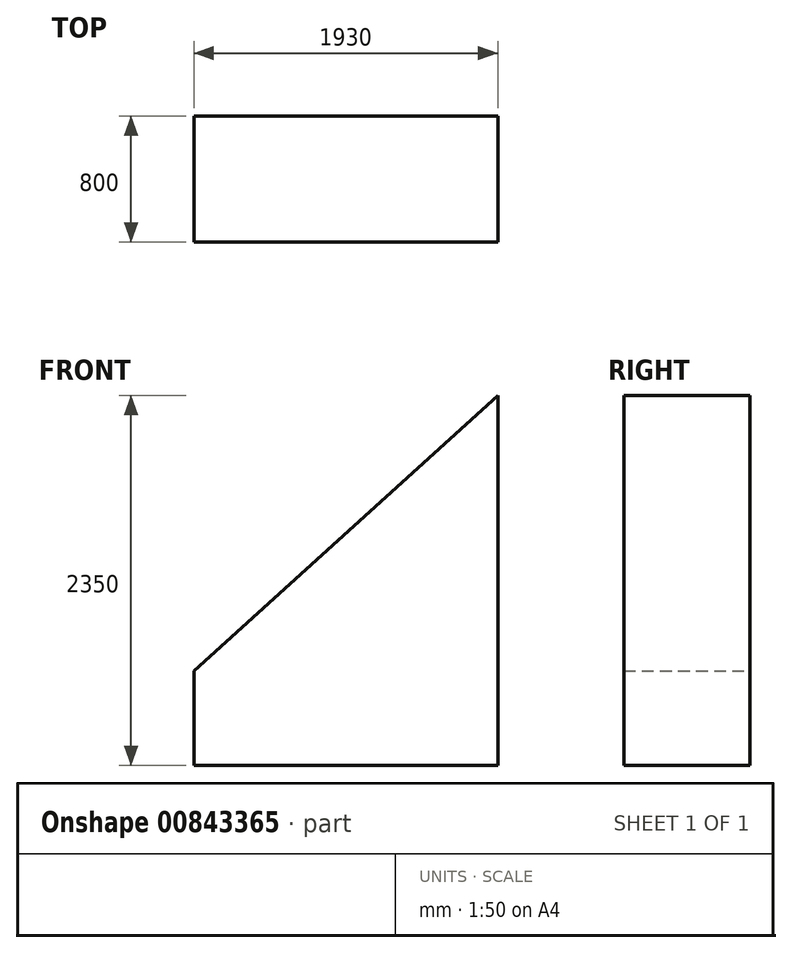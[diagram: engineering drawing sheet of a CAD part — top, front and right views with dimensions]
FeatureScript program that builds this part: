
annotation { "Feature Type Name" : "Feature", "Feature Type Description" : "" }
export const myFeature = defineFeature(function(context is Context, id is Id, definition is map)
    precondition{}
    {
        {
            var Q0;
            Q0=qCreatedBy(makeId("Front.planeOp"),FACE);
            var sketch = newSketch(context, id + "F0", { "sketchPlane" : qUnion([Q0])});
            skLineSegment(sketch, "E0", {"start": v(0, 600) * mm, "end": v(0, 0) * mm});
            skLineSegment(sketch, "E1", {"start": v(0, 0) * mm, "end": v(1930, 0) * mm});
            skLineSegment(sketch, "E2", {"start": v(1930, 2350) * mm, "end": v(0, 600) * mm});
            skLineSegment(sketch, "E3", {"start": v(1930, 2350) * mm, "end": v(1930, 0) * mm});
            skSolve(sketch);
        }
        {
            var Q0;
            Q0=makeQuery(id+"F0.imprint","IMPRINT",FACE,{"disambiguationData":[TD([[makeQuery(id+"F0.imprint","IMPRINT",EDGE,{"derivedFrom":sQuery(id+"F0.wireOp",EDGE,"E0")}),1.0]])]});
            extrude(context, id + "F1", {"entities" : qUnion([Q0]), "depth" : 800 * mm, "offsetDistance" : 25.4 * mm});
        }
    });
